# Revit family: NLRS_57_DUA_UN_rectangular-constant-volume-damper-vcmr_sacs
name_source: partatom
category: Duct Accessories
units: mm (PartAtom-declared; Revit-internal decimal feet)

## family parameters
Always vertical = No
Cut with Voids When Loaded = No
Part Type = Breaks Into
Round Connector Dimension = Use Diameter
Shared = No
Work Plane-Based = No

## types (2) — shared parameters
Assembly Code = 57.00
Description = Rectangular Volume Damper VCMR
FireRating = 0h
IfcDescription = Rectangular Volume Damper VCMR
IfcExportAs = IfcDamperType
IfcExportType = CONTROLDAMPER
LoadBearing = No
Manufacturer = Solid Air Climate Solutions
Model = Constant volume damper - Rectangular
NLRS_C_content_datum_uitgifte = 02-05-2022
NLRS_C_content_provider = Solid Air Climate Systems
NLRS_C_content_versie = Versie 3.19.00
NLRS_C_description = Rectangular Volume Damper VCMR
NLRS_C_niveau ontwikkeling = LOD400
Product_Data = VCMR_Data
SACS_Dummy = 1
Type Comments = Check flow direction!
URL = https://solid-air.nl

## per-type parameters (varying)
| type | SACS_Index2 | SACS_Type_Toggle | SACS_Z_Offset |
| Dubbelwandig  (SD) | 1 mm  [stored 0.00328084 ft] | Yes | 40 mm  [stored 0.131234 ft] |
| Enkelwandig (SO) | 0 mm  [stored 0 ft] | No | 1 mm  [stored 0.00328084 ft] |

note: [stored X ft] marks values corroborated as IEEE doubles in the binary element streams (Revit-internal decimal feet)

## geometry (parser evidence)
native form markers: Sweep x5
no freeform markers — native parametric forms only
